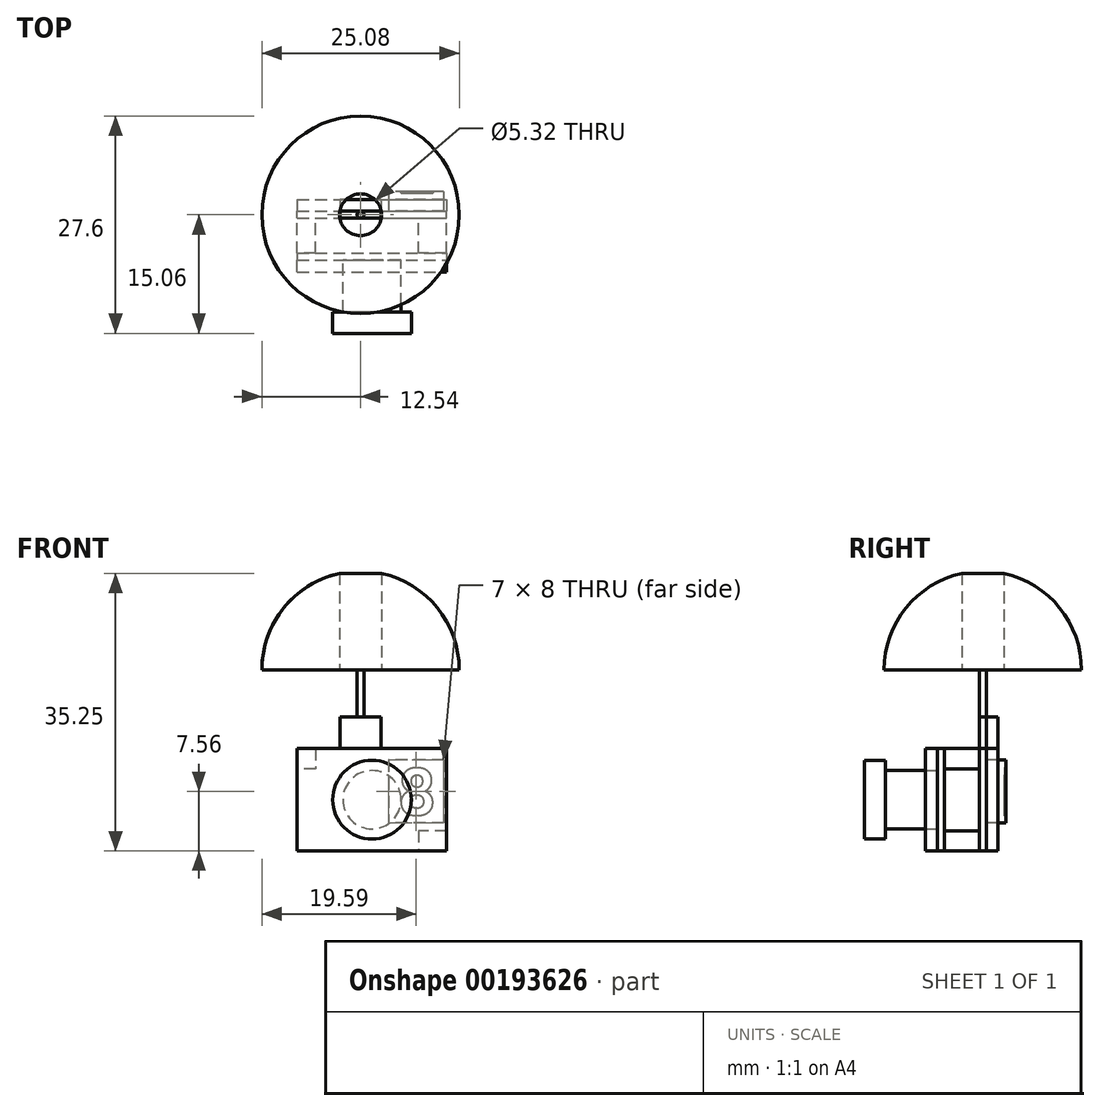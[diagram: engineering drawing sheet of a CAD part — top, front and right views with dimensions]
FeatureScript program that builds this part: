
annotation { "Feature Type Name" : "Feature", "Feature Type Description" : "" }
export const myFeature = defineFeature(function(context is Context, id is Id, definition is map)
    precondition{}
    {
        {
            var Q0;
            Q0=qCreatedBy(makeId("Top.planeOp"),FACE);
            var sketch = newSketch(context, id + "F0", { "sketchPlane" : qUnion([Q0])});
            skLineSegment(sketch, "E0", {"start": v(-9.5, 3.1) * mm, "end": v(9.5, 3.1) * mm});
            skPoint(sketch, "E1", {"position": v(0, 3.1) * mm});
            skLineSegment(sketch, "E2", {"start": v(-20.35, 0) * mm, "end": v(20, 0) * mm, "construction": true});
            skLineSegment(sketch, "E3", {"start": v(-9.5, 2.22) * mm, "end": v(9.5, 2.22) * mm});
            skLineSegment(sketch, "E4", {"start": v(9.5, 2.22) * mm, "end": v(9.5, 3.1) * mm});
            skLineSegment(sketch, "E5", {"start": v(-9.5, 2.22) * mm, "end": v(-9.5, 3.1) * mm});
            skLineSegment(sketch, "E6.MirrorCS", {"start": v(9.5, -2.22) * mm, "end": v(9.5, -3.1) * mm});
            skLineSegment(sketch, "E7.MirrorCS", {"start": v(-9.5, -2.22) * mm, "end": v(-9.5, -3.1) * mm});
            skLineSegment(sketch, "E8.MirrorCS", {"start": v(-9.5, -3.1) * mm, "end": v(9.5, -3.1) * mm});
            skLineSegment(sketch, "E9.MirrorCS", {"start": v(-9.5, -2.22) * mm, "end": v(9.5, -2.22) * mm});
            skPoint(sketch, "E10.MirrorP", {"position": v(0, -3.1) * mm});
            skSolve(sketch);
        }
        {
            var Q0;
            Q0 = qSketchRegion(id + "F0", true);
            extrude(context, id + "F1", {"entities" : qUnion([Q0]), "endBound" : BoundingType.SYMMETRIC, "depth" : 13 * mm});
        }
        {
            var Q0;
            Q0=makeQuery(id+"F1.opExtrude","SWEPT_FACE",FACE,{"disambiguationData":[OSD([sQuery(id+"F0.wireOp",EDGE,"E8.MirrorCS")])]});
            cPlane(context, id + "F2", {"entities" : qUnion([Q0]), "cplaneType" : CPlaneType.OFFSET, "offset" : 6.6 * mm, "width" : 150 * mm, "height" : 150 * mm});
        }
        {
            var Q0;
            Q0=qCreatedBy(id+"F2.planeOp",FACE);
            var sketch = newSketch(context, id + "F3", { "sketchPlane" : qUnion([Q0])});
            skCircle(sketch, "E11", {"center": v(0, 0) * mm, "radius": 5 * mm});
            skSolve(sketch);
        }
        {
            var Q0;
            Q0 = qSketchRegion(id + "F3", true);
            extrude(context, id + "F4", {"entities" : qUnion([Q0]), "depth" : 2.7 * mm});
        }
        {
            var Q0;
            Q0=makeQuery(id+"F1.opExtrude","SWEPT_FACE",FACE,{"disambiguationData":[OSD([sQuery(id+"F0.wireOp",EDGE,"E8.MirrorCS")])]});
            var sketch = newSketch(context, id + "F5", { "sketchPlane" : qUnion([Q0])});
            skCircle(sketch, "E12", {"center": v(0, 0) * mm, "radius": 3.7 * mm});
            skSolve(sketch);
        }
        {
            var Q0;
            Q0 = qSketchRegion(id + "F5", true);
            extrude(context, id + "F6", {"entities" : qUnion([Q0]), "endBound" : BoundingType.UP_TO_NEXT, "depth" : 25 * mm});
        }
        {
            var Q0;
            Q0=makeQuery(id+"F1.opExtrude","SWEPT_FACE",FACE,{"disambiguationData":[OSD([sQuery(id+"F0.wireOp",EDGE,"E3")])]});
            var sketch = newSketch(context, id + "F7", { "sketchPlane" : qUnion([Q0])});
            skLineSegment(sketch, "E13", {"start": v(9.5, -6.5) * mm, "end": v(5.9, -6.5) * mm});
            skLineSegment(sketch, "E14", {"start": v(5.9, -6.5) * mm, "end": v(5.9, -3.94) * mm});
            skLineSegment(sketch, "E15", {"start": v(5.9, -3.94) * mm, "end": v(9.5, -3.94) * mm});
            skLineSegment(sketch, "E16", {"start": v(9.5, -3.94) * mm, "end": v(9.5, -6.5) * mm});
            skLineSegment(sketch, "E17", {"start": v(-9.5, 0) * mm, "end": v(9.5, 0) * mm, "construction": true});
            skLineSegment(sketch, "E18", {"start": v(0, 6.5) * mm, "end": v(0, -6.5) * mm, "construction": true});
            skLineSegment(sketch, "E19", {"start": v(-9.5, 3.94) * mm, "end": v(-7.15, 3.94) * mm});
            skLineSegment(sketch, "E20", {"start": v(-7.15, 3.94) * mm, "end": v(-7.15, 6.5) * mm});
            skLineSegment(sketch, "E21", {"start": v(-9.5, 3.94) * mm, "end": v(-9.5, 6.5) * mm});
            skLineSegment(sketch, "E22", {"start": v(-9.5, 6.5) * mm, "end": v(-7.15, 6.5) * mm});
            skSolve(sketch);
        }
        {
            var Q0;
            Q0 = qSketchRegion(id + "F7", true);
            extrude(context, id + "F8", {"entities" : qUnion([Q0]), "endBound" : BoundingType.UP_TO_NEXT, "depth" : 25 * mm});
        }
        {
            var Q0;
            Q0=makeQuery(id+"F1.opExtrude","SWEPT_FACE",FACE,{"disambiguationData":[OSD([sQuery(id+"F0.wireOp",EDGE,"E0")])]});
            var sketch = newSketch(context, id + "F9", { "sketchPlane" : qUnion([Q0])});
            skLineSegment(sketch, "E23.bottom", {"start": v(-9.1, 5.06) * mm, "end": v(-2.1, 5.06) * mm});
            skLineSegment(sketch, "E23.top", {"start": v(-9.1, -2.94) * mm, "end": v(-2.1, -2.94) * mm});
            skLineSegment(sketch, "E23.left", {"start": v(-9.1, 5.06) * mm, "end": v(-9.1, -2.94) * mm});
            skLineSegment(sketch, "E23.right", {"start": v(-2.1, 5.06) * mm, "end": v(-2.1, -2.94) * mm});
            skSolve(sketch);
        }
        {
            var Q0;
            Q0=makeQuery(id+"F9.imprint","IMPRINT",FACE,{"disambiguationData":[TD([[makeQuery(id+"F9.imprint","IMPRINT",EDGE,{"derivedFrom":sQuery(id+"F9.wireOp",EDGE,"E23.bottom")}),-1.0]])]});
            extrude(context, id + "F10", {"entities" : qUnion([Q0]), "operationType" : NewBodyOperationType.ADD, "depth" : 2.5 * mm});
        }
        {
            var Q0;
            Q0=makeQuery(id+"F1.opExtrude","SWEPT_FACE",FACE,{"disambiguationData":[OSD([sQuery(id+"F0.wireOp",EDGE,"E0")])]});
            var sketch = newSketch(context, id + "F11", { "sketchPlane" : qUnion([Q0])});
            skLineSegment(sketch, "E24.bottom", {"start": v(-1.17, 10.5) * mm, "end": v(4.07, 10.5) * mm});
            skLineSegment(sketch, "E24.top", {"start": v(-1.17, 6.5) * mm, "end": v(4.07, 6.5) * mm});
            skLineSegment(sketch, "E24.left", {"start": v(-1.17, 10.5) * mm, "end": v(-1.17, 6.5) * mm});
            skLineSegment(sketch, "E24.right", {"start": v(4.07, 10.5) * mm, "end": v(4.07, 6.5) * mm});
            skSolve(sketch);
        }
        {
            var Q0;
            Q0=makeQuery(id+"F11.imprint","IMPRINT",FACE,{"disambiguationData":[TD([[makeQuery(id+"F11.imprint","IMPRINT",EDGE,{"derivedFrom":sQuery(id+"F11.wireOp",EDGE,"E24.bottom")}),-1.0]])]});
            var Q1;
            Q1=makeQuery(id+"F1.opExtrude","SWEPT_FACE",FACE,{"disambiguationData":[OSD([sQuery(id+"F0.wireOp",EDGE,"E3")])]});
            extrude(context, id + "F12", {"entities" : qUnion([Q0]), "operationType" : NewBodyOperationType.ADD, "endBound" : BoundingType.UP_TO_SURFACE, "oppositeDirection" : true, "endBoundEntityFace" : qUnion([Q1]), "depth" : 25 * mm});
        }
        {
            var Q0;
            Q0=makeQuery(id+"F12.opExtrude","SWEPT_FACE",FACE,{"disambiguationData":[OSD([sQuery(id+"F11.wireOp",EDGE,"E24.bottom")])]});
            var sketch = newSketch(context, id + "F13", { "sketchPlane" : qUnion([Q0])});
            skCircle(sketch, "E25", {"center": v(-1.45, 2.66) * mm, "radius": 0.44 * mm});
            skPoint(sketch, "E25.centerSnap0", {"position": v(-1.45, 3.1) * mm});
            skPoint(sketch, "E25.centerSnap1", {"position": v(1.17, 2.66) * mm});
            skSolve(sketch);
        }
        {
            var Q0;
            {var subQ0=sQuery(id+"F13.wireOp",EDGE,"E25");var subQ1=sQuery(id+"F11.wireOp",EDGE,"E24.bottom");var subQ3=makeQuery(id+"F13.imprint","INTERSECT",VERTEX,{"derivedFrom":[makeQuery(id+"F12.opExtrude","CAP_EDGE",EDGE,{"disambiguationData":[OSD([subQ1])],"isStart":true}),subQ0]});Q0=makeQuery(id+"F13.imprint","IMPRINT",FACE,{"disambiguationData":[TD([[makeQuery(id+"F13.imprint","IMPRINT",EDGE,{"disambiguationData":[TD([[subQ3,-1.0]])],"derivedFrom":subQ0}),1.0]])]});}
            extrude(context, id + "F14", {"entities" : qUnion([Q0]), "operationType" : NewBodyOperationType.ADD, "depth" : 6 * mm});
        }
        {
            var Q0;
            Q0=makeQuery(id+"F14.opExtrude","CAP_FACE",FACE,{"disambiguationData":[OSD([sQuery(id+"F13.wireOp",EDGE,"E25")])],"isStart":false});
            var sketch = newSketch(context, id + "F15", { "sketchPlane" : qUnion([Q0])});
            skCircle(sketch, "E26", {"center": v(-1.45, 2.66) * mm, "radius": 12.25 * mm});
            skSolve(sketch);
        }
        {
            var Q0;
            Q0=qCreatedBy(makeId("Front.planeOp"),FACE);
            var sketch = newSketch(context, id + "F16", { "sketchPlane" : qUnion([Q0])});
            skLineSegment(sketch, "E27", {"start": v(-1.45, 28.75) * mm, "end": v(-1.45, 16.5) * mm});
            skArc(sketch, "E28", {"start": v(-1.45, 28.75) * mm, "mid": v(-10.11, 25.16) * mm, "end": v(-13.7, 16.5) * mm});
            skLineSegment(sketch, "E29", {"start": v(-1.45, 16.5) * mm, "end": v(-13.7, 16.5) * mm});
            skLineSegment(sketch, "E30.0", {"start": v(-13.7, 16.5) * mm, "end": v(10.8, 16.5) * mm});
            skSolve(sketch);
        }
        {
            var Q0;
            {var subQ0=sQuery(id+"F16.wireOp",EDGE,"E27");Q0=makeQuery(id+"F16.imprint","IMPRINT",FACE,{"disambiguationData":[TD([[makeQuery(id+"F16.imprint","IMPRINT",EDGE,{"derivedFrom":subQ0}),-1.0]])]});}
            var Q1;
            Q1=sQuery(id+"F15.wireOp",EDGE,"E26");
            revolve(context, id + "F17", {"entities" : qUnion([Q0]), "axis" : qUnion([Q1]), "revolveType" : RevolveType.FULL});
        }
        {
            var Q0;
            Q0=makeQuery(id+"F10.opExtrude","CAP_FACE",FACE,{"disambiguationData":[OSD([sQuery(id+"F9.wireOp",EDGE,"E23.bottom"),sQuery(id+"F9.wireOp",EDGE,"E23.top"),sQuery(id+"F9.wireOp",EDGE,"E23.left"),sQuery(id+"F9.wireOp",EDGE,"E23.right")])],"isStart":false});
            var sketch = newSketch(context, id + "F18", { "sketchPlane" : qUnion([Q0])});
            skText(sketch, "E31", { "text": "8", "fontName": "RobotoSlab-Bold.ttf"});
            skPoint(sketch, "E32", {"position": v(-5.6, 1.06) * mm});
            skPoint(sketch, "E33", {"position": v(-9.1, 1.06) * mm});
            skPoint(sketch, "E34", {"position": v(-5.6, 5.06) * mm});
            const initialGuessF18  = {"E31": [-0.008, -0.00194, 1, 0, 0.006]};
            skSetInitialGuess(sketch, initialGuessF18);
            skSolve(sketch);
        }
        {
            var Q0;
            Q0=makeQuery(id+"F18.imprint","IMPRINT",FACE,{"disambiguationData":[TD([[makeQuery(id+"F18.imprint","IMPRINT",EDGE,{"derivedFrom":sQuery(id+"F18.wireOp",EDGE,"E31.sketch_text.stroke-0")}),-1.0]])]});
            extrude(context, id + "F19", {"entities" : qUnion([Q0]), "operationType" : NewBodyOperationType.REMOVE, "oppositeDirection" : true, "depth" : 0.2 * mm});
        }
        {
            var Q0;
            Q0=makeQuery(id+"F12.boolean.opBoolean","MERGE",FACE,{"derivedFrom":[makeQuery(id+"F1.opExtrude","SWEPT_FACE",FACE,{"disambiguationData":[OSD([sQuery(id+"F0.wireOp",EDGE,"E0")])]}),makeQuery(id+"F12.opExtrude","CAP_FACE",FACE,{"disambiguationData":[OSD([sQuery(id+"F11.wireOp",EDGE,"E24.bottom"),sQuery(id+"F11.wireOp",EDGE,"E24.top"),sQuery(id+"F11.wireOp",EDGE,"E24.left"),sQuery(id+"F11.wireOp",EDGE,"E24.right")])],"isStart":true})]});
            extrude(context, id + "F20", {"entities" : qUnion([Q0]), "depth" : 1.5 * mm});
        }
        {
            var Q0;
            Q0=makeQuery(id+"F1.opExtrude","SWEPT_FACE",FACE,{"disambiguationData":[OSD([sQuery(id+"F0.wireOp",EDGE,"E8.MirrorCS")])]});
            extrude(context, id + "F21", {"entities" : qUnion([Q0]), "depth" : 1.5 * mm});
        }
    });
